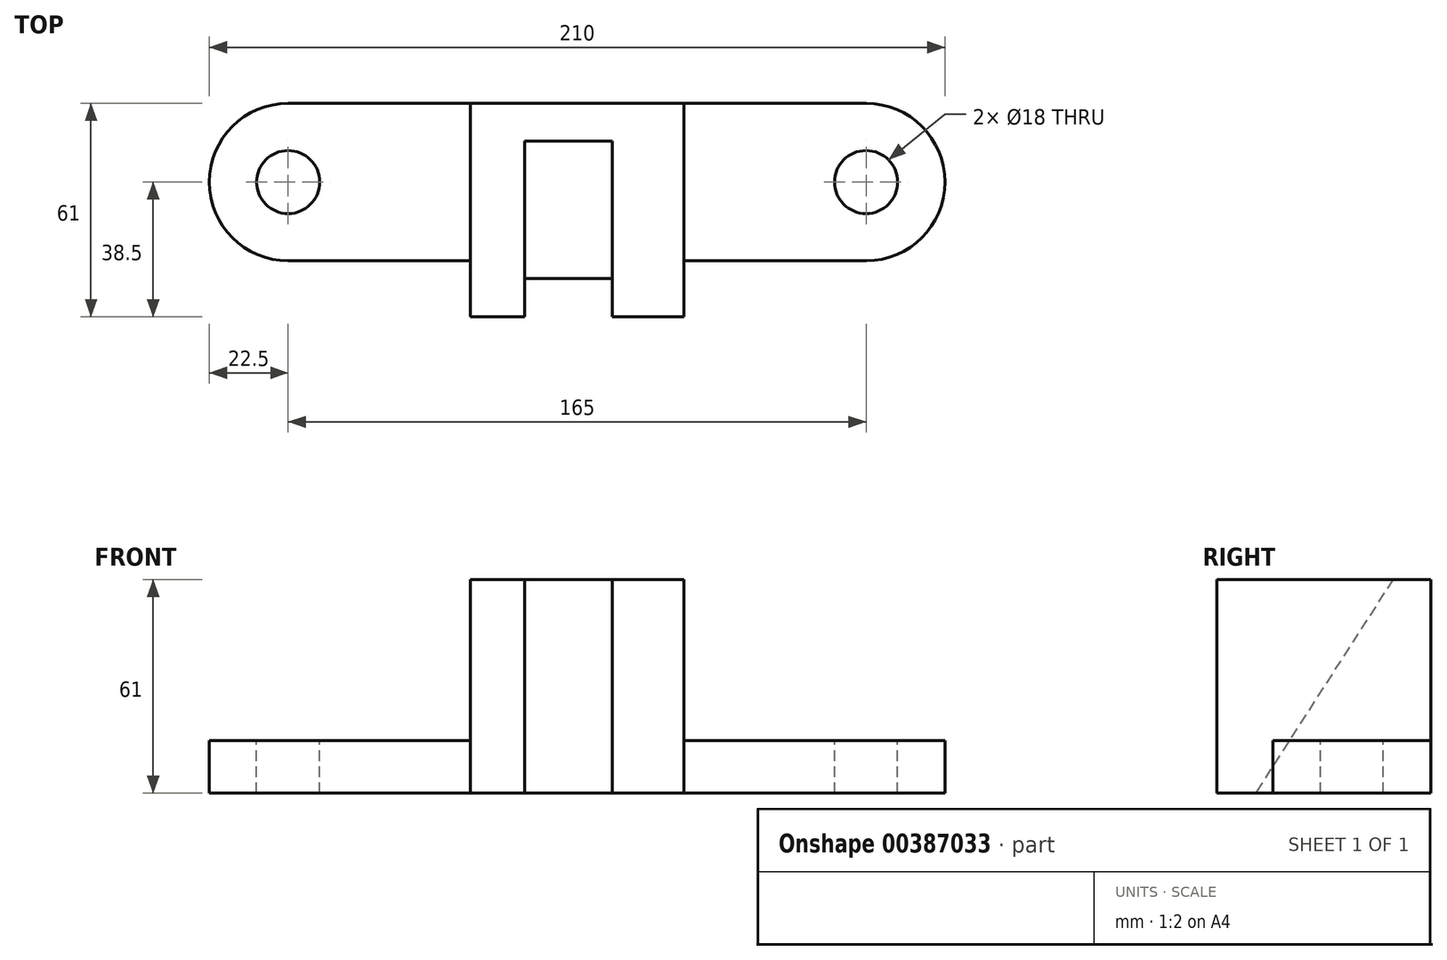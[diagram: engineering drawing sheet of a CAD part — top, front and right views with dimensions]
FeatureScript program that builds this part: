
annotation { "Feature Type Name" : "Feature", "Feature Type Description" : "" }
export const myFeature = defineFeature(function(context is Context, id is Id, definition is map)
    precondition{}
    {
        {
            var Q0;
            Q0=qCreatedBy(makeId("Front.planeOp"),FACE);
            var sketch = newSketch(context, id + "F0", { "sketchPlane" : qUnion([Q0])});
            skLineSegment(sketch, "E0.bottom", {"start": v(-30.5, 45.83) * mm, "end": v(30.5, 45.83) * mm});
            skLineSegment(sketch, "E0.top", {"start": v(-30.5, -15.17) * mm, "end": v(30.5, -15.17) * mm});
            skLineSegment(sketch, "E0.left", {"start": v(-30.5, 45.83) * mm, "end": v(-30.5, -15.17) * mm});
            skLineSegment(sketch, "E0.right", {"start": v(30.5, 45.83) * mm, "end": v(30.5, -15.17) * mm});
            skLineSegment(sketch, "E1.bottom", {"start": v(-30.5, -15.17) * mm, "end": v(-82.5, -15.17) * mm});
            skLineSegment(sketch, "E1.top", {"start": v(-30.5, -0.17) * mm, "end": v(-82.5, -0.17) * mm});
            skLineSegment(sketch, "E1.left", {"start": v(-30.5, -15.17) * mm, "end": v(-30.5, -0.17) * mm});
            skLineSegment(sketch, "E1.right", {"start": v(-82.5, -15.17) * mm, "end": v(-82.5, -0.17) * mm});
            skLineSegment(sketch, "E2.bottom", {"start": v(30.5, -15.17) * mm, "end": v(82.5, -15.17) * mm});
            skLineSegment(sketch, "E2.top", {"start": v(30.5, -0.17) * mm, "end": v(82.5, -0.17) * mm});
            skLineSegment(sketch, "E2.left", {"start": v(30.5, -15.17) * mm, "end": v(30.5, -0.17) * mm});
            skLineSegment(sketch, "E2.right", {"start": v(82.5, -15.17) * mm, "end": v(82.5, -0.17) * mm});
            skSolve(sketch);
        }
        {
            var Q0;
            Q0=makeQuery(id+"F0.imprint","IMPRINT",FACE,{"disambiguationData":[TD([[makeQuery(id+"F0.imprint","IMPRINT",EDGE,{"derivedFrom":sQuery(id+"F0.wireOp",EDGE,"E1.bottom")}),-1.0]])]});
            var Q1;
            Q1=makeQuery(id+"F0.imprint","IMPRINT",FACE,{"disambiguationData":[TD([[makeQuery(id+"F0.imprint","IMPRINT",EDGE,{"derivedFrom":sQuery(id+"F0.wireOp",EDGE,"E2.bottom")}),1.0]])]});
            extrude(context, id + "F1", {"entities" : qUnion([Q0, Q1]), "depth" : 45 * mm});
        }
        {
            var Q0;
            Q0=makeQuery(id+"F0.imprint","IMPRINT",FACE,{"disambiguationData":[TD([[makeQuery(id+"F0.imprint","IMPRINT",EDGE,{"derivedFrom":sQuery(id+"F0.wireOp",EDGE,"E0.bottom")}),-1.0]])]});
            extrude(context, id + "F2", {"entities" : qUnion([Q0]), "operationType" : NewBodyOperationType.ADD, "depth" : 61 * mm});
        }
        {
            var Q0;
            Q0=makeQuery(id+"F1.opExtrude","SWEPT_FACE",FACE,{"disambiguationData":[OSD([sQuery(id+"F0.wireOp",EDGE,"E1.top")])]});
            var sketch = newSketch(context, id + "F3", { "sketchPlane" : qUnion([Q0])});
            skCircle(sketch, "E3", {"center": v(-82.5, -22.5) * mm, "radius": 22.5 * mm});
            skCircle(sketch, "E4", {"center": v(82.5, -22.5) * mm, "radius": 22.5 * mm});
            skSolve(sketch);
        }
        {
            var Q0;
            {var subQ1=sQuery(id+"F0.wireOp",EDGE,"E1.top");var subQ2=makeQuery(id+"F1.opExtrude","SWEPT_EDGE",EDGE,{"disambiguationData":[OSD([subQ1,sQuery(id+"F0.wireOp",EDGE,"E1.right")])]});Q0=makeQuery(id+"F3.imprint","IMPRINT",FACE,{"disambiguationData":[TD([[makeQuery(id+"F3.imprint","IMPRINT",EDGE,{"derivedFrom":subQ2}),1.0]])]});}
            var Q1;
            Q1=makeQuery(id+"F3.imprint","IMPRINT",FACE,{"disambiguationData":[TD([[makeQuery(id+"F3.imprint","IMPRINT",EDGE,{"derivedFrom":sQuery(id+"F3.wireOp",EDGE,"E4")}),1.0]])]});
            extrude(context, id + "F4", {"entities" : qUnion([Q0, Q1]), "operationType" : NewBodyOperationType.ADD, "oppositeDirection" : true, "depth" : 15 * mm});
        }
        {
            var Q0;
            {var subQ0=sQuery(id+"F0.wireOp",EDGE,"E1.top");Q0=makeQuery(id+"F4.boolean.opBoolean","MERGE",FACE,{"derivedFrom":[makeQuery(id+"F1.opExtrude","SWEPT_FACE",FACE,{"disambiguationData":[OSD([subQ0])]}),makeQuery(id+"F4.opExtrude","CAP_FACE",FACE,{"disambiguationData":[OSD([subQ0,sQuery(id+"F0.wireOp",EDGE,"E1.right"),sQuery(id+"F3.wireOp",EDGE,"E3")])],"isStart":true})]});}
            var sketch = newSketch(context, id + "F5", { "sketchPlane" : qUnion([Q0])});
            skCircle(sketch, "E5", {"center": v(-82.5, -22.5) * mm, "radius": 9 * mm});
            skSolve(sketch);
        }
        {
            var Q0;
            Q0=makeQuery(id+"F4.boolean.opBoolean","MERGE",FACE,{"derivedFrom":[makeQuery(id+"F1.opExtrude","SWEPT_FACE",FACE,{"disambiguationData":[OSD([sQuery(id+"F0.wireOp",EDGE,"E2.top")])]}),makeQuery(id+"F4.opExtrude","CAP_FACE",FACE,{"disambiguationData":[OSD([sQuery(id+"F3.wireOp",EDGE,"E4")])],"isStart":true})]});
            var sketch = newSketch(context, id + "F6", { "sketchPlane" : qUnion([Q0])});
            skCircle(sketch, "E6", {"center": v(82.5, -22.5) * mm, "radius": 9 * mm});
            skSolve(sketch);
        }
        {
            var Q0;
            Q0=makeQuery(id+"F6.imprint","IMPRINT",FACE,{"disambiguationData":[TD([[makeQuery(id+"F6.imprint","IMPRINT",EDGE,{"derivedFrom":sQuery(id+"F6.wireOp",EDGE,"E6")}),1.0]])]});
            var Q1;
            Q1=makeQuery(id+"F5.imprint","IMPRINT",FACE,{"disambiguationData":[TD([[makeQuery(id+"F5.imprint","IMPRINT",EDGE,{"derivedFrom":sQuery(id+"F5.wireOp",EDGE,"E5")}),1.0]])]});
            extrude(context, id + "F7", {"entities" : qUnion([Q0, Q1]), "operationType" : NewBodyOperationType.REMOVE, "oppositeDirection" : true, "depth" : 25 * mm});
        }
        {
            var Q0;
            Q0=makeQuery(id+"F2.opExtrude","SWEPT_FACE",FACE,{"disambiguationData":[OSD([sQuery(id+"F0.wireOp",EDGE,"E0.left"),sQuery(id+"F0.wireOp",EDGE,"E1.left")])]});
            cPlane(context, id + "F8", {"entities" : qUnion([Q0]), "cplaneType" : CPlaneType.OFFSET, "offset" : 15.5 * mm, "oppositeDirection" : true, "width" : 150 * mm, "height" : 150 * mm});
        }
        {
            var Q0;
            Q0=qCreatedBy(id+"F8.planeOp",FACE);
            var sketch = newSketch(context, id + "F9", { "sketchPlane" : qUnion([Q0])});
            skLineSegment(sketch, "E7", {"start": v(10.8, 45.83) * mm, "end": v(50.04, -15.17) * mm});
            skLineSegment(sketch, "E8", {"start": v(10.8, 45.83) * mm, "end": v(61.04, 45.83) * mm});
            skLineSegment(sketch, "E9", {"start": v(61.04, 45.83) * mm, "end": v(61.04, -15.17) * mm});
            skLineSegment(sketch, "E10", {"start": v(50.04, -15.17) * mm, "end": v(61.04, -15.17) * mm});
            skPoint(sketch, "E11.end.orphan", {"position": v(3.04, 45.83) * mm});
            skPoint(sketch, "E12.end.orphan", {"position": v(3.04, -15.17) * mm});
            skSolve(sketch);
        }
        {
            var Q0;
            Q0 = qSketchRegion(id + "F9", true);
            extrude(context, id + "F10", {"entities" : qUnion([Q0]), "operationType" : NewBodyOperationType.REMOVE, "oppositeDirection" : true, "depth" : 25 * mm});
        }
    });
